# Revit family: STL23756_30 - 15°
name_source: partatom
category: Luminárias
units: mm (PartAtom-declared; Revit-internal decimal feet)

## family parameters
Com base no plano de trabalho = Não
Compartilhado = Não
Corte com vazios quando carregada = Não
Cota do conector redondo = Utilizar diâmetro
Fonte luminosa = Sim
Manter orientação da anotação = Não
Ponto de cálculo do ambiente = Não
Sempre na vertical = Sim
Tipo de parte = Normal

## types (1)
- STL23756/30 - BIVOLT - 3000K - 1500lm - 36º
    Altura do Spot = 0.12 m
    Altura do espeto à 0° = 0.43 m
    Arquivo de rede fotométrica = STELLA - STL23756-30 - ESPETO GROUND 20W SEM GRADE.ies
    Carga aparente = 0 VA
    Dimerização = Dimerização
    Diâmetro do Spot = 0.09 m
    Elevação padrão = 0 m
    Estrutura = Al - Preto
    Fabricante = Stella
    Filtro de cor = 16777215
    Fluxo Luminoso = 1500 lm
    Grau de proteção (IP) = IP67
    IRC (Índice de reprodução de cores) = >80
    Luminoso = Luminoso - 3000K
    Modelo = S.Ground
    Potência = 19 W
    Referência = STL23756/30
    Temperatura da cor (K) = 3000 K
    Tensão Elétrica = 100V-240V
    Troca de temperatura da cor de lâmpada com esmaecimento = <Nenhum>
    URL = https://stella.com.br
    Vidro = Vidro
    Ângulo de Abertura = 36°
    Ângulo de inclinação = -90.00°
